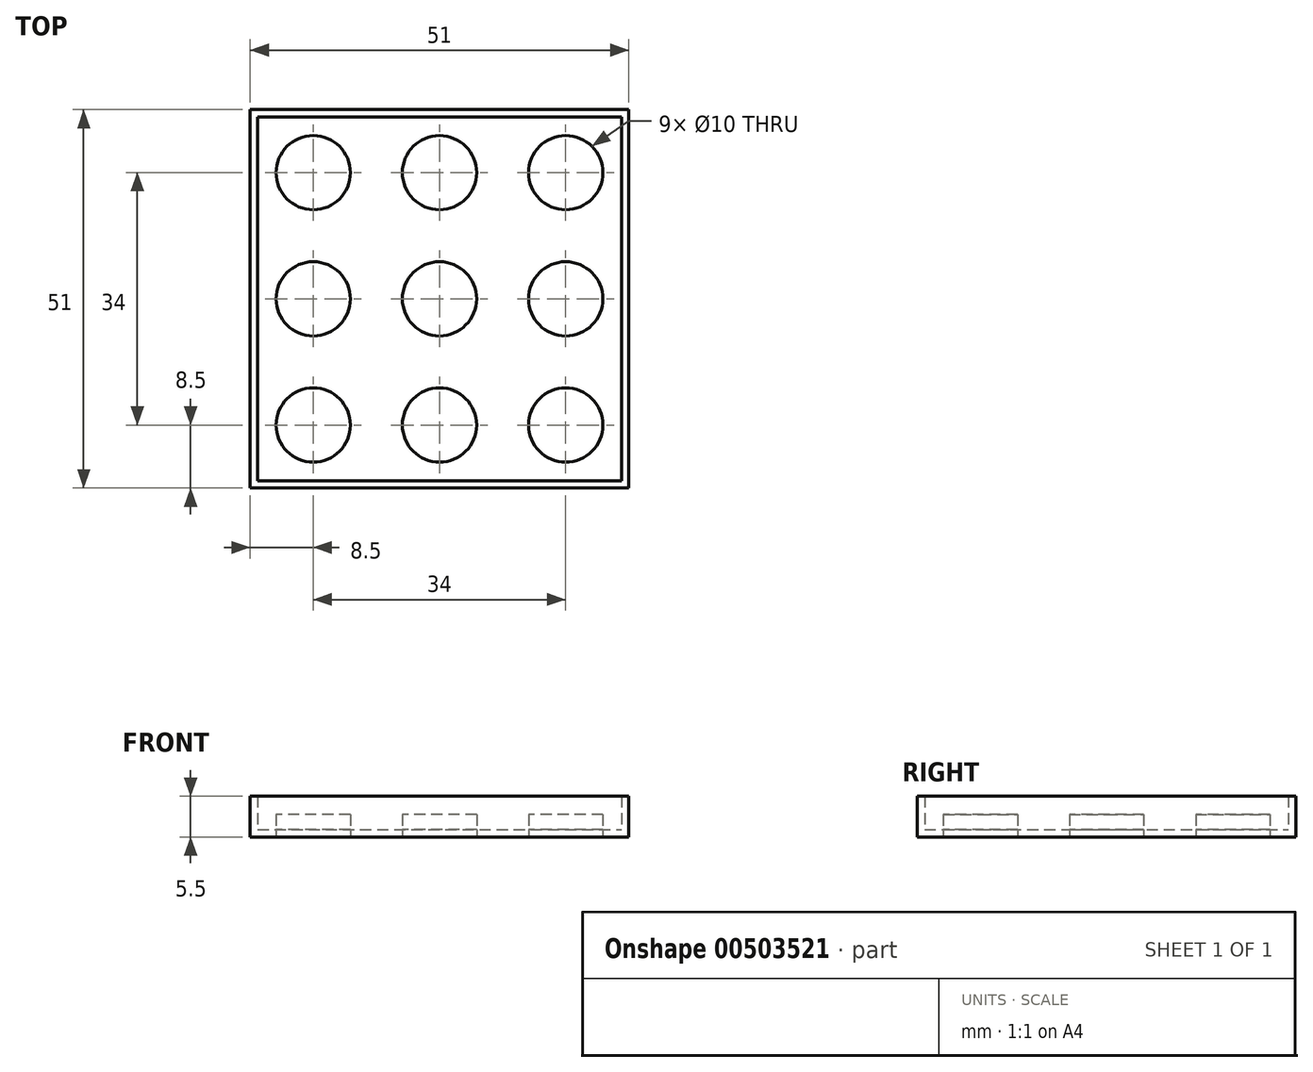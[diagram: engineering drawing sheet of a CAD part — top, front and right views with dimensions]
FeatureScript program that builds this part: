
annotation { "Feature Type Name" : "Feature", "Feature Type Description" : "" }
export const myFeature = defineFeature(function(context is Context, id is Id, definition is map)
    precondition{}
    {
        {
            var Q0;
            Q0=qCreatedBy(makeId("Top.planeOp"),FACE);
            var sketch = newSketch(context, id + "F0", { "sketchPlane" : qUnion([Q0])});
            skLineSegment(sketch, "E0.bottom", {"start": v(0, 0) * mm, "end": v(76, 0) * mm, "construction": true});
            skLineSegment(sketch, "E0.top", {"start": v(0, 76) * mm, "end": v(76, 76) * mm, "construction": true});
            skLineSegment(sketch, "E0.left", {"start": v(0, 0) * mm, "end": v(0, 76) * mm, "construction": true});
            skLineSegment(sketch, "E0.right", {"start": v(76, 0) * mm, "end": v(76, 76) * mm, "construction": true});
            skPoint(sketch, "E1", {"position": v(38, 0) * mm});
            skPoint(sketch, "E2", {"position": v(0, 38) * mm});
            skCircle(sketch, "E3", {"center": v(20.5, 20.5) * mm, "radius": 5 * mm});
            skCircle(sketch, "E4.0.1.0", {"center": v(20.5, 37.5) * mm, "radius": 5 * mm});
            skCircle(sketch, "E4.0.2.0", {"center": v(20.5, 54.5) * mm, "radius": 5 * mm});
            skCircle(sketch, "E4.1.0.0", {"center": v(37.5, 20.5) * mm, "radius": 5 * mm});
            skCircle(sketch, "E4.1.1.0", {"center": v(37.5, 37.5) * mm, "radius": 5 * mm});
            skCircle(sketch, "E4.1.2.0", {"center": v(37.5, 54.5) * mm, "radius": 5 * mm});
            skCircle(sketch, "E4.2.0.0", {"center": v(54.5, 20.5) * mm, "radius": 5 * mm});
            skCircle(sketch, "E4.2.1.0", {"center": v(54.5, 37.5) * mm, "radius": 5 * mm});
            skCircle(sketch, "E4.2.2.0", {"center": v(54.5, 54.5) * mm, "radius": 5 * mm});
            skLineSegment(sketch, "E4.direction1", {"start": v(20.5, 20.5) * mm, "end": v(37.5, 20.5) * mm, "construction": true});
            skLineSegment(sketch, "E4.direction2", {"start": v(20.5, 20.5) * mm, "end": v(20.5, 37.5) * mm, "construction": true});
            skLineSegment(sketch, "E5.bottom", {"start": v(13, 13) * mm, "end": v(62, 13) * mm});
            skLineSegment(sketch, "E5.top", {"start": v(13, 62) * mm, "end": v(62, 62) * mm});
            skLineSegment(sketch, "E5.left", {"start": v(13, 13) * mm, "end": v(13, 62) * mm});
            skLineSegment(sketch, "E5.right", {"start": v(62, 13) * mm, "end": v(62, 62) * mm});
            skLineSegment(sketch, "E6.bottom", {"start": v(12, 12) * mm, "end": v(63, 12) * mm});
            skLineSegment(sketch, "E6.top", {"start": v(12, 63) * mm, "end": v(63, 63) * mm});
            skLineSegment(sketch, "E6.left", {"start": v(12, 12) * mm, "end": v(12, 63) * mm});
            skLineSegment(sketch, "E6.right", {"start": v(63, 12) * mm, "end": v(63, 63) * mm});
            skSolve(sketch);
        }
        {
            var Q0;
            Q0=makeQuery(id+"F0.imprint","IMPRINT",FACE,{"disambiguationData":[TD([[makeQuery(id+"F0.imprint","IMPRINT",EDGE,{"derivedFrom":sQuery(id+"F0.wireOp",EDGE,"E4.0.2.0")}),1.0]])]});
            var Q1;
            Q1=makeQuery(id+"F0.imprint","IMPRINT",FACE,{"disambiguationData":[TD([[makeQuery(id+"F0.imprint","IMPRINT",EDGE,{"derivedFrom":sQuery(id+"F0.wireOp",EDGE,"E4.1.2.0")}),1.0]])]});
            var Q2;
            Q2=makeQuery(id+"F0.imprint","IMPRINT",FACE,{"disambiguationData":[TD([[makeQuery(id+"F0.imprint","IMPRINT",EDGE,{"derivedFrom":sQuery(id+"F0.wireOp",EDGE,"E4.2.2.0")}),1.0]])]});
            var Q3;
            Q3=makeQuery(id+"F0.imprint","IMPRINT",FACE,{"disambiguationData":[TD([[makeQuery(id+"F0.imprint","IMPRINT",EDGE,{"derivedFrom":sQuery(id+"F0.wireOp",EDGE,"E4.2.1.0")}),1.0]])]});
            var Q4;
            Q4=makeQuery(id+"F0.imprint","IMPRINT",FACE,{"disambiguationData":[TD([[makeQuery(id+"F0.imprint","IMPRINT",EDGE,{"derivedFrom":sQuery(id+"F0.wireOp",EDGE,"E4.1.1.0")}),1.0]])]});
            var Q5;
            Q5=makeQuery(id+"F0.imprint","IMPRINT",FACE,{"disambiguationData":[TD([[makeQuery(id+"F0.imprint","IMPRINT",EDGE,{"derivedFrom":sQuery(id+"F0.wireOp",EDGE,"E4.0.1.0")}),1.0]])]});
            var Q6;
            Q6=makeQuery(id+"F0.imprint","IMPRINT",FACE,{"disambiguationData":[TD([[makeQuery(id+"F0.imprint","IMPRINT",EDGE,{"derivedFrom":sQuery(id+"F0.wireOp",EDGE,"E3")}),1.0]])]});
            var Q7;
            Q7=makeQuery(id+"F0.imprint","IMPRINT",FACE,{"disambiguationData":[TD([[makeQuery(id+"F0.imprint","IMPRINT",EDGE,{"derivedFrom":sQuery(id+"F0.wireOp",EDGE,"E4.1.0.0")}),1.0]])]});
            var Q8;
            Q8=makeQuery(id+"F0.imprint","IMPRINT",FACE,{"disambiguationData":[TD([[makeQuery(id+"F0.imprint","IMPRINT",EDGE,{"derivedFrom":sQuery(id+"F0.wireOp",EDGE,"E4.2.0.0")}),1.0]])]});
            var Q9;
            Q9=sQuery(id+"F0.wireOp",EDGE,"E3");
            var Q10;
            Q10=sQuery(id+"F0.wireOp",EDGE,"E4.0.1.0");
            var Q11;
            Q11=sQuery(id+"F0.wireOp",EDGE,"E4.0.2.0");
            var Q12;
            Q12=sQuery(id+"F0.wireOp",EDGE,"E4.1.2.0");
            var Q13;
            Q13=sQuery(id+"F0.wireOp",EDGE,"E4.1.1.0");
            var Q14;
            Q14=sQuery(id+"F0.wireOp",EDGE,"E4.1.0.0");
            var Q15;
            Q15=sQuery(id+"F0.wireOp",EDGE,"E4.2.0.0");
            var Q16;
            Q16=sQuery(id+"F0.wireOp",EDGE,"E4.2.1.0");
            var Q17;
            Q17=sQuery(id+"F0.wireOp",EDGE,"E4.2.2.0");
            extrude(context, id + "F1", {"entities" : qUnion([Q0, Q1, Q2, Q3, Q4, Q5, Q6, Q7, Q8]), "surfaceEntities" : qUnion([Q9, Q10, Q11, Q12, Q13, Q14, Q15, Q16, Q17]), "depth" : 3 * mm});
        }
        {
            var Q0;
            Q0=makeQuery(id+"F0.imprint","IMPRINT",FACE,{"disambiguationData":[TD([[makeQuery(id+"F0.imprint","IMPRINT",EDGE,{"derivedFrom":sQuery(id+"F0.wireOp",EDGE,"E3")}),-1.0]])]});
            extrude(context, id + "F2", {"entities" : qUnion([Q0]), "depth" : 1 * mm});
        }
        {
            var Q0;
            Q0=makeQuery(id+"F0.imprint","IMPRINT",FACE,{"disambiguationData":[TD([[makeQuery(id+"F0.imprint","IMPRINT",EDGE,{"derivedFrom":sQuery(id+"F0.wireOp",EDGE,"E5.bottom")}),-1.0]])]});
            extrude(context, id + "F3", {"entities" : qUnion([Q0]), "operationType" : NewBodyOperationType.ADD, "depth" : 5.5 * mm});
        }
    });
